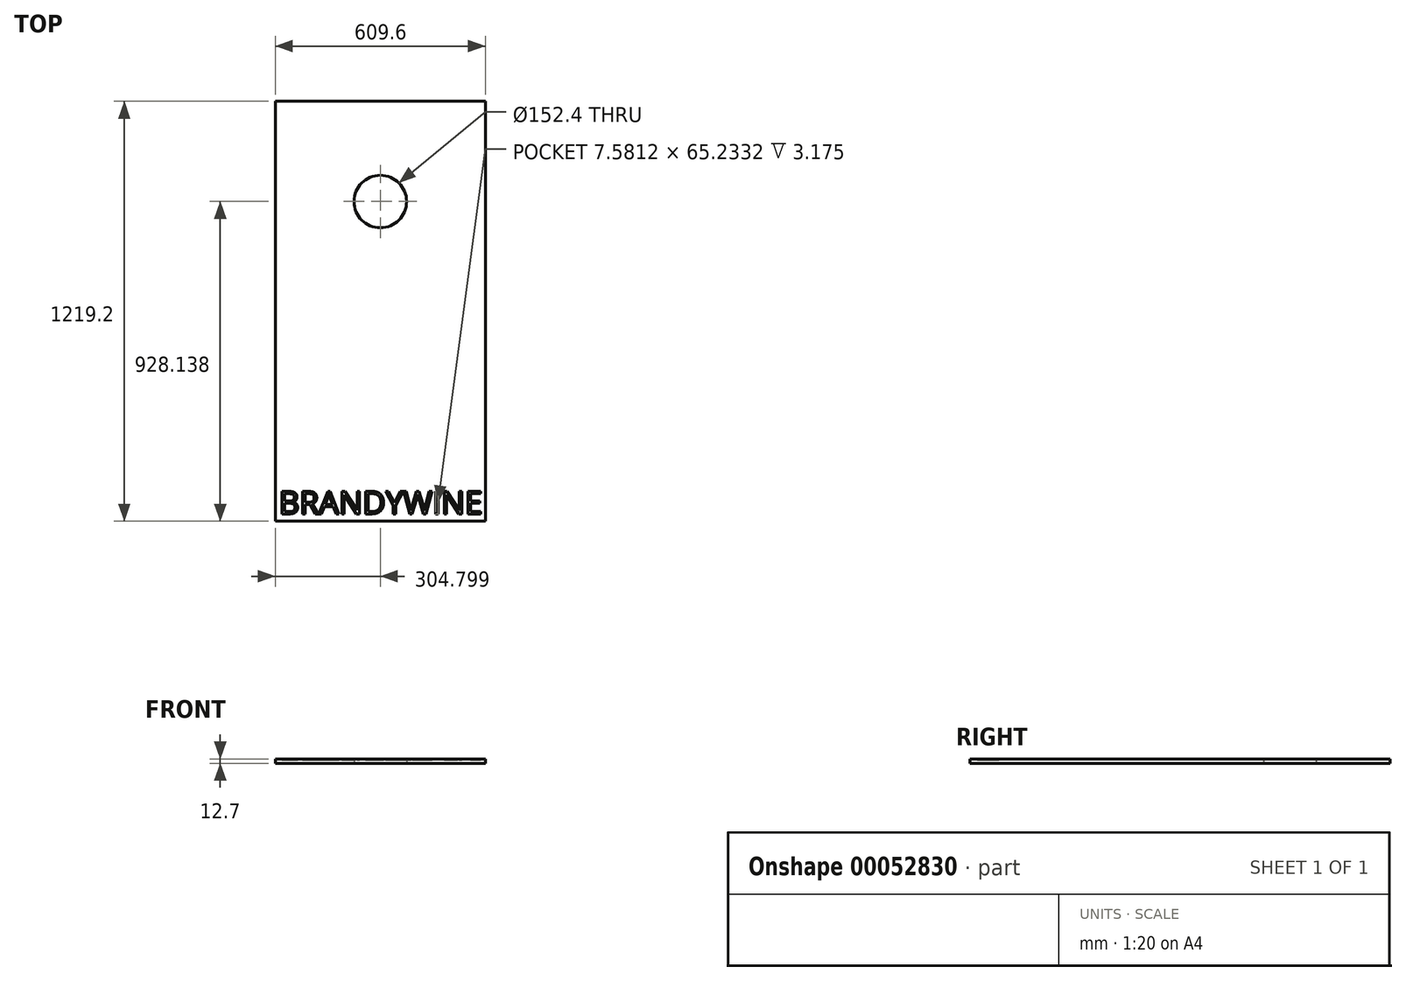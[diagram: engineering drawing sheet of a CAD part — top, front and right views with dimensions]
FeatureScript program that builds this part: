
annotation { "Feature Type Name" : "Feature", "Feature Type Description" : "" }
export const myFeature = defineFeature(function(context is Context, id is Id, definition is map)
    precondition{}
    {
        {
            var Q0;
            Q0=qCreatedBy(makeId("Top.planeOp"),FACE);
            var sketch = newSketch(context, id + "F0", { "sketchPlane" : qUnion([Q0])});
            skLineSegment(sketch, "E0.rect.bottom", {"start": v(549.96, 19.55) * mm, "end": v(-59.64, 19.55) * mm});
            skLineSegment(sketch, "E0.rect.top", {"start": v(549.96, 1238.75) * mm, "end": v(-59.64, 1238.75) * mm});
            skLineSegment(sketch, "E0.rect.left", {"start": v(549.96, 19.55) * mm, "end": v(549.96, 1238.75) * mm});
            skLineSegment(sketch, "E0.rect.right", {"start": v(-59.64, 19.55) * mm, "end": v(-59.64, 1238.75) * mm});
            skPoint(sketch, "E0.rect.middle", {"position": v(245.16, 629.15) * mm});
            skCircle(sketch, "E1", {"center": v(245.16, 947.69) * mm, "radius": 76.2 * mm});
            skPoint(sketch, "E1.centerSnap0", {"position": v(245.16, 1238.75) * mm});
            skSolve(sketch);
        }
        {
            var Q0;
            Q0=makeQuery(id+"F0.imprint","IMPRINT",FACE,{"disambiguationData":[TD([[makeQuery(id+"F0.imprint","IMPRINT",EDGE,{"derivedFrom":sQuery(id+"F0.wireOp",EDGE,"E0.rect.bottom")}),-1.0]])]});
            extrude(context, id + "F1", {"entities" : qUnion([Q0]), "depth" : 12.7 * mm});
        }
        {
            var Q0;
            Q0=makeQuery(id+"F1.opExtrude","CAP_FACE",FACE,{"disambiguationData":[OSD([sQuery(id+"F0.wireOp",EDGE,"E0.rect.bottom"),sQuery(id+"F0.wireOp",EDGE,"E0.rect.top"),sQuery(id+"F0.wireOp",EDGE,"E0.rect.left"),sQuery(id+"F0.wireOp",EDGE,"E0.rect.right"),sQuery(id+"F0.wireOp",EDGE,"E1")])],"isStart":false});
            var sketch = newSketch(context, id + "F2", { "sketchPlane" : qUnion([Q0])});
            skText(sketch, "E2", { "text": "BRANDYWINE", "fontName": "OpenSans-Regular.ttf"});
            const initialGuessF2  = {"E2": [-0.04877, 0.04082, 1, 0, 0.06579]};
            skSetInitialGuess(sketch, initialGuessF2);
            skSolve(sketch);
        }
        {
            var Q0;
            Q0 = qSketchRegion(id + "F2", true);
            extrude(context, id + "F3", {"entities" : qUnion([Q0]), "operationType" : NewBodyOperationType.REMOVE, "oppositeDirection" : true, "depth" : 3.17 * mm});
        }
    });
